# Revit family: Building-Materials_Glass-Glazing_Vitro-Architectural-Glass_Optiblue-Glass
name_source: partatom
category: Curtain Panels
units: mm (PartAtom-declared; Revit-internal decimal feet)

## family parameters
Always vertical = Yes
Classification Number = 23.25.20.14.11.11.17
Cut with Voids When Loaded = No
Shared = No

## types (3) — shared parameters
1st Lite Thickness = 0' - 0 1/4"
2nd Lite Thickness = 0' - 0 1/4"
Airspace Thickness = 0' - 0 1/2"
Analytic Construction = Low-E double glazing (1/4 in + 1/4 in)
Assembly Code = B2020220
Define Thermal Properties by = Schematic Type
Description = Optiblue® glass is a light-bodied, neutral color tint that optimizes the performance and aesthetics of Solarban® glass coatings as substrates.
Finish = Glass
Heat Transfer Coefficient (U) = 0.29 BTU/(h·ft²·°F)
Interior Glass Material = Vitro Architectural-Glass - Clear
Keynote = 08900
Manufacturer = Vitro Architectural Glass
Product Guid = a833fc07-8210-4d2f-8438-37bb3653fa00
Product Page URL = https://www.vitroglazings.com
Product data url = https://www.bimobject.com
Thermal Resistance (R) = 8.3333 (h·ft²·°F)/BTU
Total Thickness = 0' - 1"
U-Value Argon (Winter Night) = 0.24 BTU/(h·ft²·°F)
URL = https://www.vitroglazings.com

## per-type parameters (varying)
| type | Exterior Glass Material | Glass Code | ISO Damage Weighted Transmittance | Light to Solar Gain | Reflectance (Visible Exterior) | Reflectance (Visible Interior) | Shadow Coefficient | Solar Heat Gain Coefficient | Solar Light Transmittance | U-Value Air (Summer Day) | U-Value Air (Winter Night) | U-Value Argon (Summer Day) | UV Light Transmittance | Visual Light Transmittance |
| Solarban 90 (2) Optiblue + Clear | Vitro Architectural-Glass - Solarban 90 (2) Optiblue | 3 | 0.279 | 1.85 | 8 | 19 | 0.22 | 0.2 | 0.14 | 0.27 BTU/(h·ft²·°F) | 0.29 BTU/(h·ft²·°F) | 0.21 BTU/(h·ft²·°F) | 0.05 | 0.37 |
| Solarban 60/z50 (2) Optiblue + Clear | Vitro Architectural-Glass - Solarban 60 (2) Optiblue | 1 | 0.418 | 1.59 | 8 | 11 | 0.37 | 0.32 | 0.26 | 0.27 BTU/(h·ft²·°F) | 0.29 BTU/(h·ft²·°F) | 0.22 BTU/(h·ft²·°F) | 0.14 | 0.51 |
| Solarban 70/z75 (2) Optiblue + Clear | Vitro Architectural-Glass - Solarban 70 (2) Optiblue | 2 | 0.337 | 2 | 9 | 13 | 0.26 | 0.23 | 0.18 | 0.26 BTU/(h·ft²·°F) | 0.28 BTU/(h·ft²·°F) | 0.21 BTU/(h·ft²·°F) | 0.05 | 0.46 |

note: column(s) folded — value = type name in every type: Model

## geometry (parser evidence)
native form markers: Sweep x1
no freeform markers — native parametric forms only
